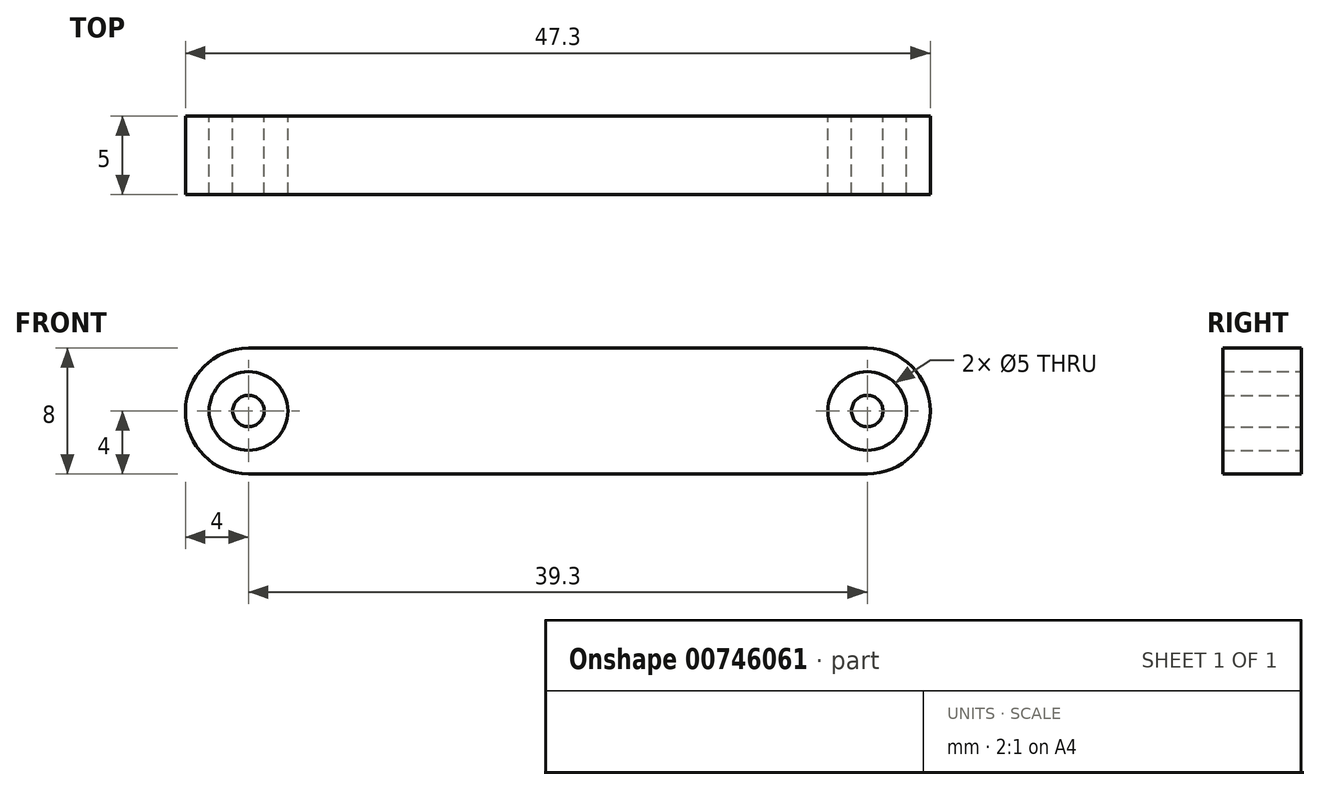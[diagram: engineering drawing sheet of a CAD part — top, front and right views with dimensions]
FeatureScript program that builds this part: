
annotation { "Feature Type Name" : "Feature", "Feature Type Description" : "" }
export const myFeature = defineFeature(function(context is Context, id is Id, definition is map)
    precondition{}
    {
        {
            var Q0;
            Q0=qCreatedBy(makeId("Front.planeOp"),FACE);
            var sketch = newSketch(context, id + "F0", { "sketchPlane" : qUnion([Q0])});
            skCircle(sketch, "E0", {"center": v(0, 0) * mm, "radius": 2.5 * mm});
            skArc(sketch, "E1", {"start": v(0, 4) * mm, "mid": v(-4, 0) * mm, "end": v(0, -4) * mm});
            skCircle(sketch, "E2", {"center": v(0, 0) * mm, "radius": 1 * mm});
            skCircle(sketch, "E3", {"center": v(39.3, 0) * mm, "radius": 2.5 * mm});
            skArc(sketch, "E4", {"start": v(39.3, -4) * mm, "mid": v(43.3, 0) * mm, "end": v(39.3, 4) * mm});
            skCircle(sketch, "E5", {"center": v(39.3, 0) * mm, "radius": 1 * mm});
            skLineSegment(sketch, "E6", {"start": v(0, 4) * mm, "end": v(39.3, 4) * mm});
            skLineSegment(sketch, "E7", {"start": v(0, -4) * mm, "end": v(39.3, -4) * mm});
            skSolve(sketch);
        }
        {
            var Q0;
            Q0=makeQuery(id+"F0.imprint","IMPRINT",FACE,{"disambiguationData":[TD([[makeQuery(id+"F0.imprint","IMPRINT",EDGE,{"derivedFrom":sQuery(id+"F0.wireOp",EDGE,"E2")}),1.0]])]});
            var Q1;
            Q1=makeQuery(id+"F0.imprint","IMPRINT",FACE,{"disambiguationData":[TD([[makeQuery(id+"F0.imprint","IMPRINT",EDGE,{"derivedFrom":sQuery(id+"F0.wireOp",EDGE,"E0")}),-1.0]])]});
            var Q2;
            Q2=makeQuery(id+"F0.imprint","IMPRINT",FACE,{"disambiguationData":[TD([[makeQuery(id+"F0.imprint","IMPRINT",EDGE,{"derivedFrom":sQuery(id+"F0.wireOp",EDGE,"E5")}),1.0]])]});
            extrude(context, id + "F1", {"entities" : qUnion([Q0, Q1, Q2]), "depth" : 5 * mm, "offsetDistance" : 25 * mm});
        }
    });
